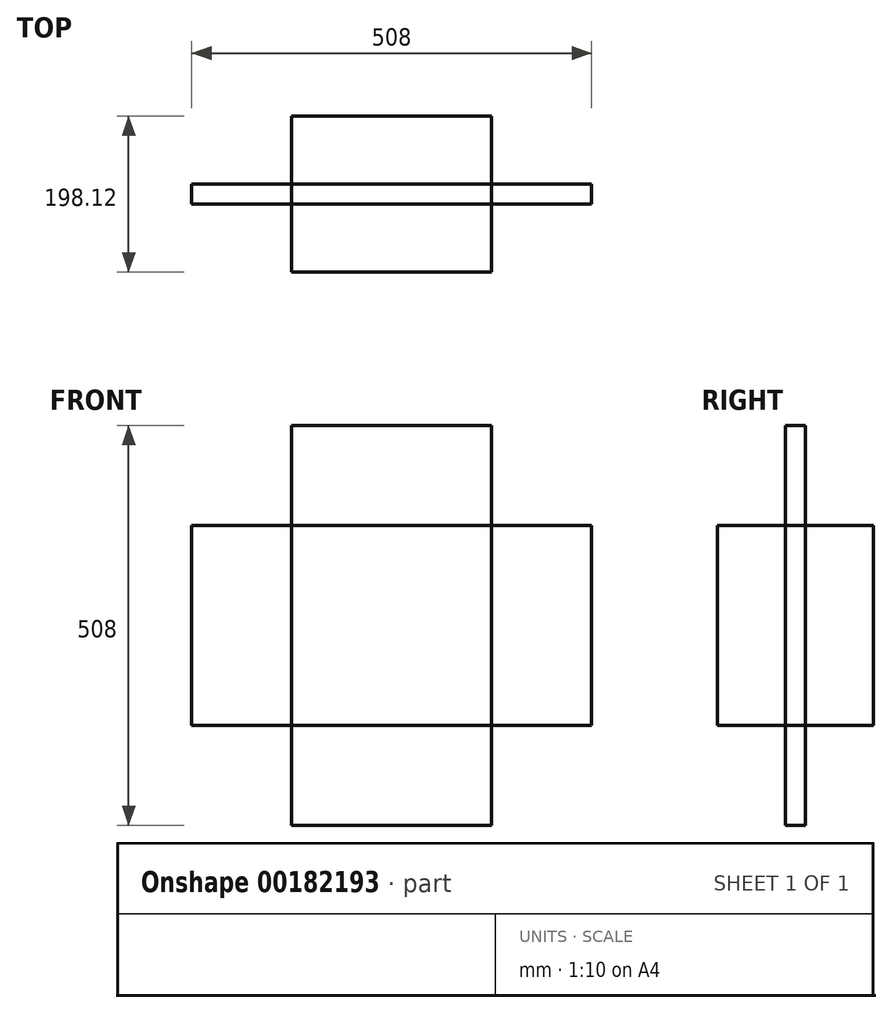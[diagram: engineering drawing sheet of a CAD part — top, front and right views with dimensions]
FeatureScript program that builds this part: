
annotation { "Feature Type Name" : "Feature", "Feature Type Description" : "" }
export const myFeature = defineFeature(function(context is Context, id is Id, definition is map)
    precondition{}
    {
        {
            var Q0;
            Q0=qCreatedBy(makeId("Front.planeOp"),FACE);
            var sketch = newSketch(context, id + "F0", { "sketchPlane" : qUnion([Q0])});
            skLineSegment(sketch, "E0", {"start": v(-254, 0) * mm, "end": v(-254, 127) * mm});
            skLineSegment(sketch, "E1.MirrorCS", {"start": v(254, 0) * mm, "end": v(254, 127) * mm});
            skLineSegment(sketch, "E2", {"start": v(-254, 127) * mm, "end": v(-127, 127) * mm});
            skLineSegment(sketch, "E3", {"start": v(-127, 127) * mm, "end": v(-127, 254) * mm});
            skLineSegment(sketch, "E4.MirrorCS", {"start": v(254, 127) * mm, "end": v(127, 127) * mm});
            skLineSegment(sketch, "E5.MirrorCS", {"start": v(127, 127) * mm, "end": v(127, 254) * mm});
            skLineSegment(sketch, "E6", {"start": v(-127, 254) * mm, "end": v(0, 254) * mm});
            skLineSegment(sketch, "E7.MirrorCS", {"start": v(127, 254) * mm, "end": v(0, 254) * mm});
            skLineSegment(sketch, "E8.MirrorCS", {"start": v(-254, 0) * mm, "end": v(-254, -127) * mm});
            skLineSegment(sketch, "E9.MirrorCS", {"start": v(254, 0) * mm, "end": v(254, -127) * mm});
            skLineSegment(sketch, "E10.MirrorCS", {"start": v(-254, -127) * mm, "end": v(-127, -127) * mm});
            skLineSegment(sketch, "E11.MirrorCS", {"start": v(-127, -127) * mm, "end": v(-127, -254) * mm});
            skLineSegment(sketch, "E12.MirrorCS", {"start": v(-127, -254) * mm, "end": v(0, -254) * mm});
            skLineSegment(sketch, "E13.MirrorCS", {"start": v(127, -254) * mm, "end": v(0, -254) * mm});
            skLineSegment(sketch, "E14.MirrorCS", {"start": v(127, -127) * mm, "end": v(127, -254) * mm});
            skLineSegment(sketch, "E15.MirrorCS", {"start": v(254, -127) * mm, "end": v(127, -127) * mm});
            skLineSegment(sketch, "E16", {"start": v(-127, 127) * mm, "end": v(127, 127) * mm});
            skLineSegment(sketch, "E17", {"start": v(127, -127) * mm, "end": v(127, 127) * mm});
            skLineSegment(sketch, "E18", {"start": v(-127, -127) * mm, "end": v(127, -127) * mm});
            skLineSegment(sketch, "E19", {"start": v(-127, -127) * mm, "end": v(-127, 127) * mm});
            skSolve(sketch);
        }
        {
            var Q0;
            Q0=makeQuery(id+"F0.imprint","IMPRINT",FACE,{"disambiguationData":[TD([[makeQuery(id+"F0.imprint","IMPRINT",EDGE,{"derivedFrom":sQuery(id+"F0.wireOp",EDGE,"E3")}),-1.0]])]});
            var Q1;
            Q1=makeQuery(id+"F0.imprint","IMPRINT",FACE,{"disambiguationData":[TD([[makeQuery(id+"F0.imprint","IMPRINT",EDGE,{"derivedFrom":sQuery(id+"F0.wireOp",EDGE,"E0")}),-1.0]])]});
            var Q2;
            Q2=makeQuery(id+"F0.imprint","IMPRINT",FACE,{"disambiguationData":[TD([[makeQuery(id+"F0.imprint","IMPRINT",EDGE,{"derivedFrom":sQuery(id+"F0.wireOp",EDGE,"E11.MirrorCS")}),1.0]])]});
            var Q3;
            Q3=makeQuery(id+"F0.imprint","IMPRINT",FACE,{"disambiguationData":[TD([[makeQuery(id+"F0.imprint","IMPRINT",EDGE,{"derivedFrom":sQuery(id+"F0.wireOp",EDGE,"E1.MirrorCS")}),1.0]])]});
            extrude(context, id + "F1", {"entities" : qUnion([Q0, Q1, Q2, Q3]), "endBound" : BoundingType.SYMMETRIC, "depth" : 25.4 * mm});
        }
        {
            var Q0;
            Q0=makeQuery(id+"F0.imprint","IMPRINT",FACE,{"disambiguationData":[TD([[makeQuery(id+"F0.imprint","IMPRINT",EDGE,{"derivedFrom":sQuery(id+"F0.wireOp",EDGE,"E16")}),-1.0]])]});
            extrude(context, id + "F2", {"entities" : qUnion([Q0]), "endBound" : BoundingType.SYMMETRIC, "depth" : 198.12 * mm});
        }
    });
